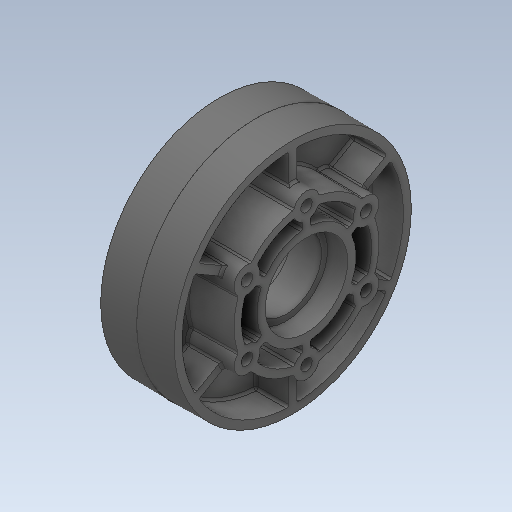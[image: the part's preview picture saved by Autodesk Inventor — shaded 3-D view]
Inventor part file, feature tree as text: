
AUTODESK INVENTOR PART (.ipt)
format: ipt  version: 2020 (Build 240168000, 168)  size: 1,228,288 bytes
history: native  units: in
note: dims shown in document units (in); Inventor stores cm internally (conversion verified against a paired STEP export)
features: fillet x2
ambient origin geometry x8: Origin, YZ Plane, XZ Plane, XY Plane, X Axis, Y Axis, Z Axis, Center Point
bodies: Solid1 (feature_tree), Solid2 (feature_tree)
feature tree (2):
  fillet  "Fillet10"  [1 undecoded]
  fillet  "Fillet9"  [1 undecoded]
note: 2 required parameter values undecoded (feature->parameter linkage not recoverable at this tier; creation-order binding heuristic only, values carry confidence <= 0.55)
